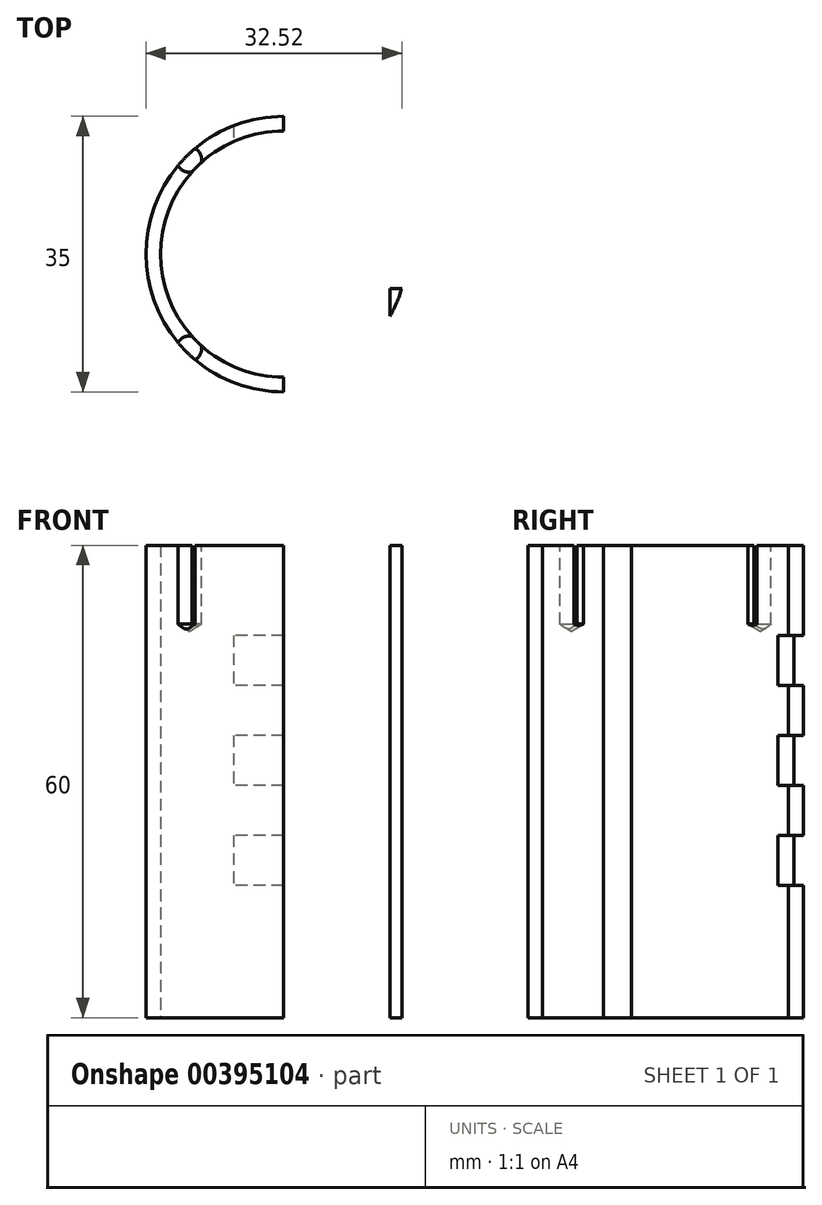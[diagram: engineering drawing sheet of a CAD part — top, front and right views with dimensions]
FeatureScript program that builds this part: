
annotation { "Feature Type Name" : "Feature", "Feature Type Description" : "" }
export const myFeature = defineFeature(function(context is Context, id is Id, definition is map)
    precondition{}
    {
        {
            var Q0;
            Q0=qCreatedBy(makeId("Top.planeOp"),FACE);
            var sketch = newSketch(context, id + "F0", { "sketchPlane" : qUnion([Q0])});
            skArc(sketch, "E0", {"start": v(0, 15.64) * mm, "mid": v(-15.64, 0) * mm, "end": v(0, -15.64) * mm});
            skLineSegment(sketch, "E1", {"start": v(-15.02, -4.36) * mm, "end": v(0, -4.36) * mm});
            skLineSegment(sketch, "E2", {"start": v(0, -4.36) * mm, "end": v(0, 15.64) * mm});
            skArc(sketch, "E3", {"start": v(0, 17.5) * mm, "mid": v(-17.5, 0) * mm, "end": v(0, -17.5) * mm});
            skLineSegment(sketch, "E4", {"start": v(-15.02, -4.36) * mm, "end": v(-13.52, -4.36) * mm});
            skLineSegment(sketch, "E5", {"start": v(-13.52, -4.36) * mm, "end": v(-13.52, -7.86) * mm});
            skPoint(sketch, "E6", {"position": v(0, -15.64) * mm});
            skPoint(sketch, "E7", {"position": v(0, -17.5) * mm});
            skPoint(sketch, "E8", {"position": v(0, 17.5) * mm});
            skLineSegment(sketch, "E9", {"start": v(0, 17.5) * mm, "end": v(0, -17.5) * mm});
            skArc(sketch, "E10.MirrorCS", {"start": v(0, 15.64) * mm, "mid": v(15.64, 0) * mm, "end": v(0, -15.64) * mm});
            skArc(sketch, "E11.MirrorCS", {"start": v(0, 17.5) * mm, "mid": v(17.5, 0) * mm, "end": v(0, -17.5) * mm});
            skLineSegment(sketch, "E12.MirrorCS", {"start": v(13.52, -4.36) * mm, "end": v(13.52, -7.86) * mm});
            skLineSegment(sketch, "E13.MirrorCS", {"start": v(15.02, -4.36) * mm, "end": v(13.52, -4.36) * mm});
            skSolve(sketch);
        }
        {
            var Q0;
            Q0=makeQuery(id+"F0.imprint","IMPRINT",FACE,{"disambiguationData":[TD([[makeQuery(id+"F0.imprint","IMPRINT",EDGE,{"derivedFrom":sQuery(id+"F0.wireOp",EDGE,"E3")}),1.0]])]});
            var Q1;
            {var subQ6=sQuery(id+"F0.wireOp",EDGE,"E11.MirrorCS");Q1=makeQuery(id+"F0.imprint","IMPRINT",FACE,{"disambiguationData":[TD([[makeQuery(id+"F0.imprint","IMPRINT",EDGE,{"derivedFrom":subQ6}),-1.0]])]});}
            extrude(context, id + "F1", {"entities" : qUnion([Q0, Q1]), "depth" : 60 * mm});
        }
        {
            var Q0;
            {var subQ0=sQuery(id+"F0.wireOp",EDGE,"E4");Q0=makeQuery(id+"F0.imprint","IMPRINT",FACE,{"disambiguationData":[TD([[makeQuery(id+"F0.imprint","IMPRINT",EDGE,{"derivedFrom":subQ0}),-1.0]])]});}
            var Q1;
            {var subQ0=sQuery(id+"F0.wireOp",EDGE,"E12.MirrorCS");Q1=makeQuery(id+"F0.imprint","IMPRINT",FACE,{"disambiguationData":[TD([[makeQuery(id+"F0.imprint","IMPRINT",EDGE,{"derivedFrom":subQ0}),1.0]])]});}
            extrude(context, id + "F2", {"entities" : qUnion([Q0, Q1]), "operationType" : NewBodyOperationType.ADD, "depth" : 60 * mm});
        }
        {
            var Q0;
            {var subQ0=sQuery(id+"F0.wireOp",EDGE,"E10.MirrorCS");var subQ1=sQuery(id+"F0.wireOp",EDGE,"E0");Q0=makeQuery(id+"F2.boolean.opBoolean","MERGE",FACE,{"derivedFrom":[makeQuery(id+"F1.opExtrude","CAP_FACE",FACE,{"disambiguationData":[OSD([subQ1,sQuery(id+"F0.wireOp",EDGE,"E3"),subQ0,sQuery(id+"F0.wireOp",EDGE,"E11.MirrorCS")])],"isStart":false}),makeQuery(id+"F2.opExtrude","CAP_FACE",FACE,{"disambiguationData":[OSD([subQ1,sQuery(id+"F0.wireOp",EDGE,"E4"),sQuery(id+"F0.wireOp",EDGE,"E5")])],"isStart":false}),makeQuery(id+"F2.opExtrude","CAP_FACE",FACE,{"disambiguationData":[OSD([subQ0,sQuery(id+"F0.wireOp",EDGE,"E12.MirrorCS"),sQuery(id+"F0.wireOp",EDGE,"E13.MirrorCS")])],"isStart":false})]});}
            var sketch = newSketch(context, id + "F3", { "sketchPlane" : qUnion([Q0])});
            skPoint(sketch, "E14", {"position": v(0, 0) * mm});
            skLineSegment(sketch, "E15.bottom", {"start": v(12, 12) * mm, "end": v(-12, 12) * mm});
            skLineSegment(sketch, "E15.top", {"start": v(12, -12) * mm, "end": v(-12, -12) * mm});
            skLineSegment(sketch, "E15.left", {"start": v(12, 12) * mm, "end": v(12, -12) * mm});
            skLineSegment(sketch, "E15.right", {"start": v(-12, 12) * mm, "end": v(-12, -12) * mm});
            skSolve(sketch);
        }
        {
            var Q0;
            Q0=sQuery(id+"F3.wireOp",VERTEX,"E15.left.start");
            var Q1;
            Q1=sQuery(id+"F3.wireOp",VERTEX,"E15.right.start");
            var Q2;
            Q2=sQuery(id+"F3.wireOp",VERTEX,"E15.right.end");
            var Q3;
            Q3=sQuery(id+"F3.wireOp",VERTEX,"E15.left.end");
            var Q4;
            Q4=makeQuery(id+"F1.opExtrude","SWEPT_BODY",BODY,{"disambiguationData":[OSD([sQuery(id+"F0.wireOp",EDGE,"E0"),sQuery(id+"F0.wireOp",EDGE,"E3"),sQuery(id+"F0.wireOp",EDGE,"E10.MirrorCS"),sQuery(id+"F0.wireOp",EDGE,"E11.MirrorCS")])]});
            hole(context, id + "F4", {"style" : HoleStyle.SIMPLE, "endStyle" : HoleEndStyle.BLIND, "holeDiameter" : 3.2 * mm, "holeDepth" : 10 * mm, "isTappedThrough" : true, "tappedDepth" : 12 * mm, "tapClearance" : 3, "locations" : qUnion([Q0, Q1, Q2, Q3]), "scope" : qUnion([Q4])});
        }
        {
            var Q0;
            Q0=qCreatedBy(makeId("Front.planeOp"),FACE);
            var sketch = newSketch(context, id + "F5", { "sketchPlane" : qUnion([Q0])});
            skLineSegment(sketch, "E16", {"start": v(0, 0) * mm, "end": v(0, 128.29) * mm});
            skPoint(sketch, "E17", {"position": v(0, 20) * mm});
            skPoint(sketch, "E18", {"position": v(0, 32.7) * mm});
            skPoint(sketch, "E19", {"position": v(0, 45.4) * mm});
            skLineSegment(sketch, "E20.bottom", {"start": v(6.35, 23.18) * mm, "end": v(-6.35, 23.18) * mm});
            skLineSegment(sketch, "E20.top", {"start": v(6.35, 16.82) * mm, "end": v(-6.35, 16.82) * mm});
            skLineSegment(sketch, "E20.left", {"start": v(6.35, 23.18) * mm, "end": v(6.35, 16.82) * mm});
            skLineSegment(sketch, "E20.right", {"start": v(-6.35, 23.18) * mm, "end": v(-6.35, 16.82) * mm});
            skLineSegment(sketch, "E21.bottom", {"start": v(6.35, 35.88) * mm, "end": v(-6.35, 35.88) * mm});
            skLineSegment(sketch, "E21.top", {"start": v(6.35, 29.53) * mm, "end": v(-6.35, 29.53) * mm});
            skLineSegment(sketch, "E21.left", {"start": v(6.35, 35.88) * mm, "end": v(6.35, 29.52) * mm});
            skLineSegment(sketch, "E21.right", {"start": v(-6.35, 35.88) * mm, "end": v(-6.35, 29.53) * mm});
            skLineSegment(sketch, "E22.bottom", {"start": v(6.35, 48.58) * mm, "end": v(-6.35, 48.58) * mm});
            skLineSegment(sketch, "E22.top", {"start": v(6.35, 42.23) * mm, "end": v(-6.35, 42.23) * mm});
            skLineSegment(sketch, "E22.left", {"start": v(6.35, 48.58) * mm, "end": v(6.35, 42.23) * mm});
            skLineSegment(sketch, "E22.right", {"start": v(-6.35, 48.58) * mm, "end": v(-6.35, 42.23) * mm});
            skSolve(sketch);
        }
        {
            var Q0;
            Q0 = qSketchRegion(id + "F5", true);
            extrude(context, id + "F6", {"entities" : qUnion([Q0]), "operationType" : NewBodyOperationType.REMOVE, "oppositeDirection" : true, "depth" : 25 * mm});
        }
    });
